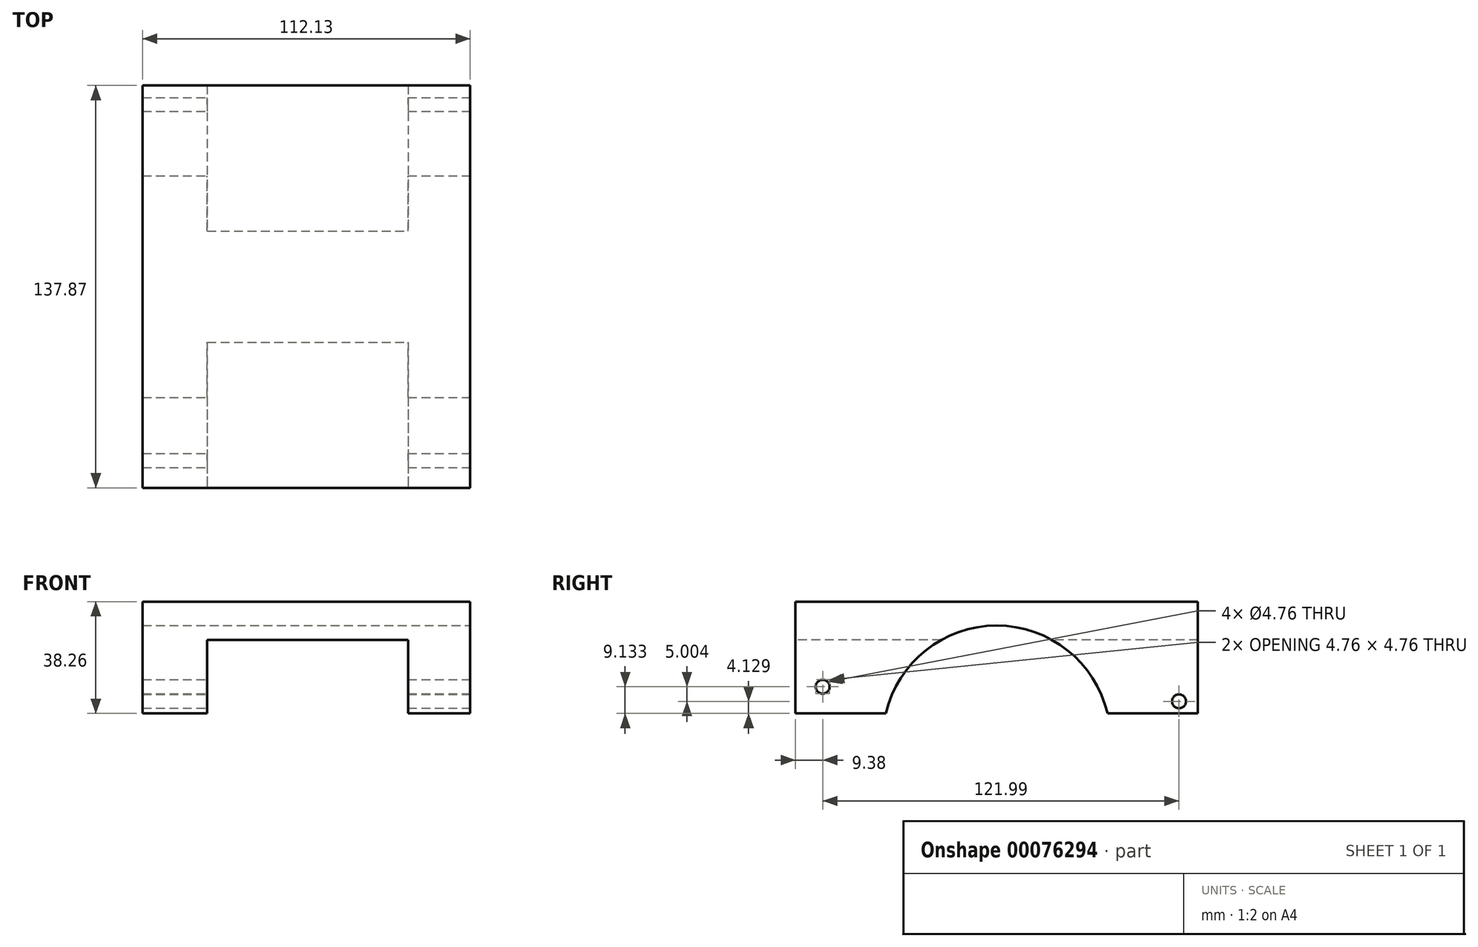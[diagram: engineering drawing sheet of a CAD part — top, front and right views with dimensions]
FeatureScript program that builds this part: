
annotation { "Feature Type Name" : "Feature", "Feature Type Description" : "" }
export const myFeature = defineFeature(function(context is Context, id is Id, definition is map)
    precondition{}
    {
        {
            var Q0;
            Q0=qCreatedBy(makeId("Front.planeOp"),FACE);
            var sketch = newSketch(context, id + "F0", { "sketchPlane" : qUnion([Q0])});
            skLineSegment(sketch, "E0.bottom", {"start": v(-57.39, 38.26) * mm, "end": v(54.74, 38.26) * mm});
            skLineSegment(sketch, "E0.top", {"start": v(-57.39, 0) * mm, "end": v(54.74, 0) * mm});
            skLineSegment(sketch, "E0.left", {"start": v(-57.39, 38.26) * mm, "end": v(-57.39, 0) * mm});
            skLineSegment(sketch, "E0.right", {"start": v(54.74, 38.26) * mm, "end": v(54.74, 0) * mm});
            skSolve(sketch);
        }
        {
            var Q0;
            Q0=makeQuery(id+"F0.imprint","IMPRINT",FACE,{"disambiguationData":[TD([[makeQuery(id+"F0.imprint","IMPRINT",EDGE,{"derivedFrom":sQuery(id+"F0.wireOp",EDGE,"E0.bottom")}),-1.0]])]});
            extrude(context, id + "F1", {"entities" : qUnion([Q0]), "depth" : 137.87 * mm});
        }
        {
            var Q0;
            Q0=makeQuery(id+"F1.opExtrude","CAP_FACE",FACE,{"disambiguationData":[OSD([sQuery(id+"F0.wireOp",EDGE,"E0.bottom"),sQuery(id+"F0.wireOp",EDGE,"E0.top"),sQuery(id+"F0.wireOp",EDGE,"E0.left"),sQuery(id+"F0.wireOp",EDGE,"E0.right")])],"isStart":false});
            var sketch = newSketch(context, id + "F2", { "sketchPlane" : qUnion([Q0])});
            skLineSegment(sketch, "E1.bottom", {"start": v(-35.27, 25.15) * mm, "end": v(33.51, 25.15) * mm});
            skLineSegment(sketch, "E1.top", {"start": v(-35.27, 0) * mm, "end": v(33.51, 0) * mm});
            skLineSegment(sketch, "E1.left", {"start": v(-35.27, 25.15) * mm, "end": v(-35.27, 0) * mm});
            skLineSegment(sketch, "E1.right", {"start": v(33.51, 25.15) * mm, "end": v(33.51, 0) * mm});
            skSolve(sketch);
        }
        {
            var Q0;
            Q0=makeQuery(id+"F2.imprint","IMPRINT",FACE,{"disambiguationData":[TD([[makeQuery(id+"F2.imprint","IMPRINT",EDGE,{"derivedFrom":sQuery(id+"F2.wireOp",EDGE,"E1.bottom")}),-1.0]])]});
            extrude(context, id + "F3", {"entities" : qUnion([Q0]), "operationType" : NewBodyOperationType.REMOVE, "endBound" : BoundingType.THROUGH_ALL, "oppositeDirection" : true, "depth" : 25.4 * mm});
        }
        {
            var Q0;
            Q0=makeQuery(id+"F1.opExtrude","SWEPT_FACE",FACE,{"disambiguationData":[OSD([sQuery(id+"F0.wireOp",EDGE,"E0.right")])]});
            var sketch = newSketch(context, id + "F4", { "sketchPlane" : qUnion([Q0])});
            skCircle(sketch, "E2", {"center": v(-128.5, 9.13) * mm, "radius": 2.38 * mm});
            skSolve(sketch);
        }
        {
            var Q0;
            Q0=makeQuery(id+"F4.imprint","IMPRINT",FACE,{"disambiguationData":[TD([[makeQuery(id+"F4.imprint","IMPRINT",EDGE,{"derivedFrom":sQuery(id+"F4.wireOp",EDGE,"E2")}),1.0]])]});
            extrude(context, id + "F5", {"entities" : qUnion([Q0]), "operationType" : NewBodyOperationType.REMOVE, "endBound" : BoundingType.THROUGH_ALL, "oppositeDirection" : true, "depth" : 25.4 * mm});
        }
        {
            var Q0;
            Q0=makeQuery(id+"F1.opExtrude","SWEPT_FACE",FACE,{"disambiguationData":[OSD([sQuery(id+"F0.wireOp",EDGE,"E0.right")])]});
            var sketch = newSketch(context, id + "F6", { "sketchPlane" : qUnion([Q0])});
            skCircle(sketch, "E3", {"center": v(-6.5, 4.13) * mm, "radius": 2.38 * mm});
            skSolve(sketch);
        }
        {
            var Q0;
            Q0=makeQuery(id+"F6.imprint","IMPRINT",FACE,{"disambiguationData":[TD([[makeQuery(id+"F6.imprint","IMPRINT",EDGE,{"derivedFrom":sQuery(id+"F6.wireOp",EDGE,"E3")}),1.0]])]});
            extrude(context, id + "F7", {"entities" : qUnion([Q0]), "operationType" : NewBodyOperationType.REMOVE, "endBound" : BoundingType.THROUGH_ALL, "oppositeDirection" : true, "depth" : 25.4 * mm});
        }
        {
            var Q0;
            Q0=makeQuery(id+"F1.opExtrude","SWEPT_FACE",FACE,{"disambiguationData":[OSD([sQuery(id+"F0.wireOp",EDGE,"E0.right")])]});
            var sketch = newSketch(context, id + "F8", { "sketchPlane" : qUnion([Q0])});
            skCircle(sketch, "E4", {"center": v(-68.94, -8.9) * mm, "radius": 39 * mm});
            skPoint(sketch, "E4.centerSnap0", {"position": v(-68.94, 0) * mm});
            skSolve(sketch);
        }
        {
            var Q0;
            {var subQ0=sQuery(id+"F8.wireOp",EDGE,"E4");var subQ1=makeQuery(id+"F1.opExtrude","SWEPT_EDGE",EDGE,{"disambiguationData":[OSD([sQuery(id+"F0.wireOp",EDGE,"E0.top"),sQuery(id+"F0.wireOp",EDGE,"E0.right")])]});var subQ2=makeQuery(id+"F8.imprint","INTERSECT",VERTEX,{"disambiguationData":[OD(0.0)],"derivedFrom":[subQ1,subQ0]});Q0=makeQuery(id+"F8.imprint","IMPRINT",FACE,{"disambiguationData":[TD([[makeQuery(id+"F8.imprint","IMPRINT",EDGE,{"disambiguationData":[TD([[subQ2,-1.0]])],"derivedFrom":subQ0}),1.0]])]});}
            extrude(context, id + "F9", {"entities" : qUnion([Q0]), "operationType" : NewBodyOperationType.REMOVE, "endBound" : BoundingType.THROUGH_ALL, "oppositeDirection" : true, "depth" : 25.4 * mm});
        }
    });
